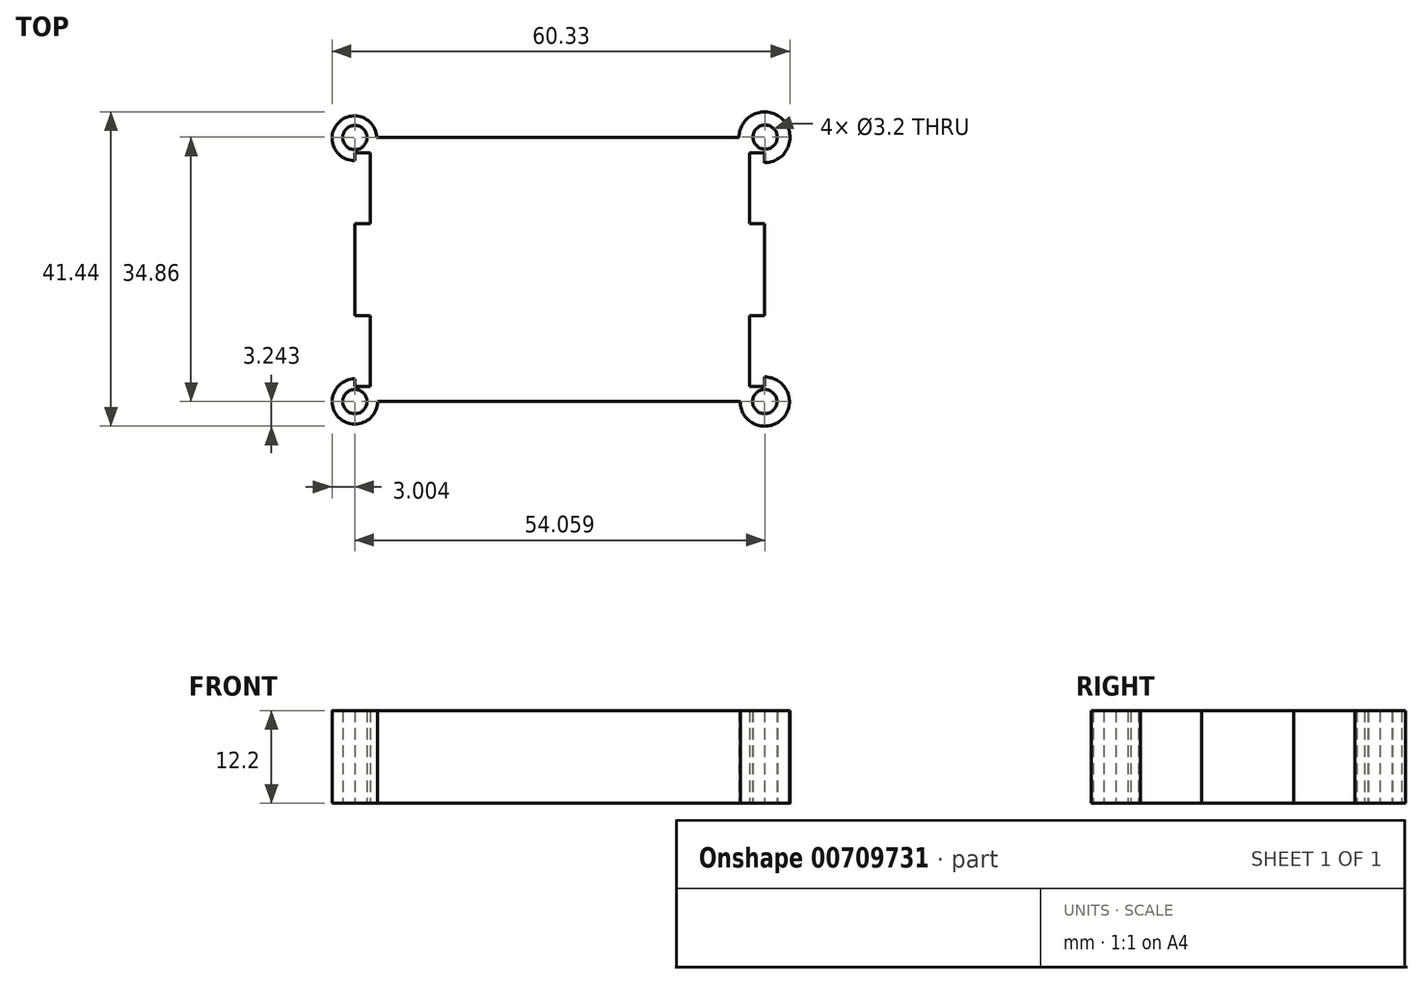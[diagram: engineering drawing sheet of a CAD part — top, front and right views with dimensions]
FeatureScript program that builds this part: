
annotation { "Feature Type Name" : "Feature", "Feature Type Description" : "" }
export const myFeature = defineFeature(function(context is Context, id is Id, definition is map)
    precondition{}
    {
        {
            var Q0;
            Q0=qCreatedBy(makeId("Top.planeOp"),FACE);
            var sketch = newSketch(context, id + "F0", { "sketchPlane" : qUnion([Q0])});
            skLineSegment(sketch, "E0.bottom", {"start": v(-28.95, 12.73) * mm, "end": v(25.05, 12.73) * mm});
            skLineSegment(sketch, "E0.top", {"start": v(-28.95, -22.07) * mm, "end": v(25.05, -22.07) * mm});
            skLineSegment(sketch, "E0.left", {"start": v(-28.95, 12.73) * mm, "end": v(-28.95, -22.07) * mm});
            skLineSegment(sketch, "E0.right", {"start": v(25.05, 12.73) * mm, "end": v(25.05, -22.07) * mm});
            skLineSegment(sketch, "E1", {"start": v(-28.95, 10.73) * mm, "end": v(25.05, 10.73) * mm});
            skLineSegment(sketch, "E2", {"start": v(-28.95, -20.07) * mm, "end": v(25.05, -20.07) * mm});
            skLineSegment(sketch, "E3.bottom", {"start": v(-28.95, 1.4) * mm, "end": v(25.05, 1.4) * mm});
            skLineSegment(sketch, "E3.top", {"start": v(-28.95, 0) * mm, "end": v(25.05, 0) * mm});
            skLineSegment(sketch, "E3.left", {"start": v(-28.95, 1.4) * mm, "end": v(-28.95, 0) * mm});
            skLineSegment(sketch, "E3.right", {"start": v(25.05, 1.4) * mm, "end": v(25.05, 0) * mm});
            skLineSegment(sketch, "E4.bottom", {"start": v(-28.95, -9.33) * mm, "end": v(25.05, -9.33) * mm});
            skLineSegment(sketch, "E4.top", {"start": v(-28.95, -10.73) * mm, "end": v(25.05, -10.73) * mm});
            skLineSegment(sketch, "E4.left", {"start": v(-28.95, -9.33) * mm, "end": v(-28.95, -10.73) * mm});
            skLineSegment(sketch, "E4.right", {"start": v(25.05, -9.33) * mm, "end": v(25.05, -10.73) * mm});
            skLineSegment(sketch, "E5.bottom", {"start": v(-28.95, 12.73) * mm, "end": v(-26.95, 12.73) * mm});
            skLineSegment(sketch, "E5.top", {"start": v(-28.95, -22.07) * mm, "end": v(-26.95, -22.07) * mm});
            skLineSegment(sketch, "E5.right", {"start": v(-26.95, 12.73) * mm, "end": v(-26.95, -22.07) * mm});
            skLineSegment(sketch, "E6.bottom", {"start": v(25.05, 12.73) * mm, "end": v(23.05, 12.73) * mm});
            skLineSegment(sketch, "E6.top", {"start": v(25.05, -22.07) * mm, "end": v(23.05, -22.07) * mm});
            skLineSegment(sketch, "E7", {"start": v(23.05, 12.73) * mm, "end": v(23.05, -22.07) * mm});
            skCircle(sketch, "E8", {"center": v(-28.95, 12.73) * mm, "radius": 1.6 * mm});
            skCircle(sketch, "E9", {"center": v(-28.95, -22.07) * mm, "radius": 1.6 * mm});
            skCircle(sketch, "E10", {"center": v(25.05, -22.07) * mm, "radius": 1.6 * mm});
            skCircle(sketch, "E11", {"center": v(25.11, 12.8) * mm, "radius": 1.6 * mm});
            skArc(sketch, "E12", {"start": v(-26.06, 12.73) * mm, "mid": v(-31.14, 14.68) * mm, "end": v(-28.95, 9.7) * mm});
            skArc(sketch, "E13", {"start": v(21.82, -22.07) * mm, "mid": v(27.36, -24.35) * mm, "end": v(25.05, -18.82) * mm});
            skArc(sketch, "E14", {"start": v(-28.95, -19.06) * mm, "mid": v(-31.08, -24.15) * mm, "end": v(-25.97, -22.07) * mm});
            skArc(sketch, "E15", {"start": v(25.05, 9.42) * mm, "mid": v(27.37, 15.17) * mm, "end": v(21.67, 12.73) * mm});
            skSolve(sketch);
        }
        {
            var Q0;
            {var subQ2=sQuery(id+"F0.wireOp",EDGE,"E13");Q0=makeQuery(id+"F0.imprint","IMPRINT",FACE,{"disambiguationData":[TD([[makeQuery(id+"F0.imprint","IMPRINT",EDGE,{"derivedFrom":subQ2}),1.0]])]});}
            var Q1;
            {var subQ0=sQuery(id+"F0.wireOp",EDGE,"E5.right");var subQ1=sQuery(id+"F0.wireOp",EDGE,"E3.bottom");var subQ2=makeQuery(id+"F0.imprint","INTERSECT",VERTEX,{"derivedFrom":[subQ1,subQ0]});Q1=makeQuery(id+"F0.imprint","IMPRINT",FACE,{"disambiguationData":[TD([[makeQuery(id+"F0.imprint","IMPRINT",EDGE,{"disambiguationData":[TD([[subQ2,-1.0]])],"derivedFrom":subQ1}),-1.0]])]});}
            var Q2;
            {var subQ3=sQuery(id+"F0.wireOp",EDGE,"E1");var subQ5=sQuery(id+"F0.wireOp",EDGE,"E0.left");var subQ6=makeQuery(id+"F0.imprint","INTERSECT",VERTEX,{"derivedFrom":[subQ3,subQ5]});Q2=makeQuery(id+"F0.imprint","IMPRINT",FACE,{"disambiguationData":[TD([[makeQuery(id+"F0.imprint","IMPRINT",EDGE,{"disambiguationData":[TD([[subQ6,-1.0]])],"derivedFrom":subQ3}),1.0]])]});}
            var Q3;
            {var subQ3=sQuery(id+"F0.wireOp",EDGE,"E2");var subQ5=sQuery(id+"F0.wireOp",EDGE,"E0.left");var subQ6=makeQuery(id+"F0.imprint","INTERSECT",VERTEX,{"derivedFrom":[subQ3,subQ5]});Q3=makeQuery(id+"F0.imprint","IMPRINT",FACE,{"disambiguationData":[TD([[makeQuery(id+"F0.imprint","IMPRINT",EDGE,{"disambiguationData":[TD([[subQ6,-1.0]])],"derivedFrom":subQ3}),-1.0]])]});}
            var Q4;
            {var subQ3=sQuery(id+"F0.wireOp",EDGE,"E1");var subQ5=sQuery(id+"F0.wireOp",EDGE,"E0.right");var subQ6=makeQuery(id+"F0.imprint","INTERSECT",VERTEX,{"derivedFrom":[subQ3,subQ5]});Q4=makeQuery(id+"F0.imprint","IMPRINT",FACE,{"disambiguationData":[TD([[makeQuery(id+"F0.imprint","IMPRINT",EDGE,{"disambiguationData":[TD([[subQ6,1.0]])],"derivedFrom":subQ3}),1.0]])]});}
            var Q5;
            {var subQ0=sQuery(id+"F0.wireOp",EDGE,"E5.right");var subQ1=sQuery(id+"F0.wireOp",EDGE,"E1");var subQ2=makeQuery(id+"F0.imprint","INTERSECT",VERTEX,{"derivedFrom":[subQ1,subQ0]});Q5=makeQuery(id+"F0.imprint","IMPRINT",FACE,{"disambiguationData":[TD([[makeQuery(id+"F0.imprint","IMPRINT",EDGE,{"disambiguationData":[TD([[subQ2,-1.0]])],"derivedFrom":subQ1}),-1.0]])]});}
            var Q6;
            {var subQ0=sQuery(id+"F0.wireOp",EDGE,"E0.left");var subQ1=sQuery(id+"F0.wireOp",EDGE,"E1");var subQ2=makeQuery(id+"F0.imprint","INTERSECT",VERTEX,{"derivedFrom":[subQ1,subQ0]});Q6=makeQuery(id+"F0.imprint","IMPRINT",FACE,{"disambiguationData":[TD([[makeQuery(id+"F0.imprint","IMPRINT",EDGE,{"disambiguationData":[TD([[subQ2,-1.0]])],"derivedFrom":subQ1}),-1.0]])]});}
            var Q7;
            {var subQ0=sQuery(id+"F0.wireOp",EDGE,"E5.right");var subQ1=sQuery(id+"F0.wireOp",EDGE,"E3.top");var subQ2=makeQuery(id+"F0.imprint","INTERSECT",VERTEX,{"derivedFrom":[subQ1,subQ0]});Q7=makeQuery(id+"F0.imprint","IMPRINT",FACE,{"disambiguationData":[TD([[makeQuery(id+"F0.imprint","IMPRINT",EDGE,{"disambiguationData":[TD([[subQ2,-1.0]])],"derivedFrom":subQ1}),-1.0]])]});}
            var Q8;
            {var subQ4=sQuery(id+"F0.wireOp",EDGE,"E15");Q8=makeQuery(id+"F0.imprint","IMPRINT",FACE,{"disambiguationData":[TD([[makeQuery(id+"F0.imprint","IMPRINT",EDGE,{"derivedFrom":subQ4}),1.0]])]});}
            var Q9;
            {var subQ0=sQuery(id+"F0.wireOp",EDGE,"E0.right");var subQ1=sQuery(id+"F0.wireOp",EDGE,"E4.bottom");var subQ2=makeQuery(id+"F0.imprint","INTERSECT",VERTEX,{"derivedFrom":[subQ1,subQ0]});Q9=makeQuery(id+"F0.imprint","IMPRINT",FACE,{"disambiguationData":[TD([[makeQuery(id+"F0.imprint","IMPRINT",EDGE,{"disambiguationData":[TD([[subQ2,1.0]])],"derivedFrom":subQ1}),-1.0]])]});}
            var Q10;
            {var subQ4=sQuery(id+"F0.wireOp",EDGE,"E12");Q10=makeQuery(id+"F0.imprint","IMPRINT",FACE,{"disambiguationData":[TD([[makeQuery(id+"F0.imprint","IMPRINT",EDGE,{"derivedFrom":subQ4}),1.0]])]});}
            var Q11;
            {var subQ2=sQuery(id+"F0.wireOp",EDGE,"E14");Q11=makeQuery(id+"F0.imprint","IMPRINT",FACE,{"disambiguationData":[TD([[makeQuery(id+"F0.imprint","IMPRINT",EDGE,{"derivedFrom":subQ2}),1.0]])]});}
            var Q12;
            {var subQ5=sQuery(id+"F0.wireOp",EDGE,"E0.bottom");var subQ8=makeQuery(id+"F0.imprint","INTERSECT",VERTEX,{"derivedFrom":[subQ5,sQuery(id+"F0.wireOp",EDGE,"E12")]});Q12=makeQuery(id+"F0.imprint","IMPRINT",FACE,{"disambiguationData":[TD([[makeQuery(id+"F0.imprint","IMPRINT",EDGE,{"disambiguationData":[TD([[subQ8,-1.0]])],"derivedFrom":subQ5}),-1.0]])]});}
            var Q13;
            {var subQ5=sQuery(id+"F0.wireOp",EDGE,"E0.top");var subQ7=makeQuery(id+"F0.imprint","INTERSECT",VERTEX,{"derivedFrom":[subQ5,sQuery(id+"F0.wireOp",EDGE,"E13")]});Q13=makeQuery(id+"F0.imprint","IMPRINT",FACE,{"disambiguationData":[TD([[makeQuery(id+"F0.imprint","IMPRINT",EDGE,{"disambiguationData":[TD([[subQ7,1.0]])],"derivedFrom":subQ5}),1.0]])]});}
            var Q14;
            {var subQ0=sQuery(id+"F0.wireOp",EDGE,"E0.left");var subQ1=sQuery(id+"F0.wireOp",EDGE,"E3.bottom");var subQ2=makeQuery(id+"F0.imprint","INTERSECT",VERTEX,{"derivedFrom":[subQ1,subQ0]});Q14=makeQuery(id+"F0.imprint","IMPRINT",FACE,{"disambiguationData":[TD([[makeQuery(id+"F0.imprint","IMPRINT",EDGE,{"disambiguationData":[TD([[subQ2,-1.0]])],"derivedFrom":subQ1}),-1.0]])]});}
            var Q15;
            {var subQ0=sQuery(id+"F0.wireOp",EDGE,"E0.right");var subQ1=sQuery(id+"F0.wireOp",EDGE,"E3.bottom");var subQ2=makeQuery(id+"F0.imprint","INTERSECT",VERTEX,{"derivedFrom":[subQ1,subQ0]});Q15=makeQuery(id+"F0.imprint","IMPRINT",FACE,{"disambiguationData":[TD([[makeQuery(id+"F0.imprint","IMPRINT",EDGE,{"disambiguationData":[TD([[subQ2,1.0]])],"derivedFrom":subQ1}),-1.0]])]});}
            var Q16;
            {var subQ0=sQuery(id+"F0.wireOp",EDGE,"E0.left");var subQ1=sQuery(id+"F0.wireOp",EDGE,"E3.top");var subQ2=makeQuery(id+"F0.imprint","INTERSECT",VERTEX,{"derivedFrom":[subQ1,subQ0]});Q16=makeQuery(id+"F0.imprint","IMPRINT",FACE,{"disambiguationData":[TD([[makeQuery(id+"F0.imprint","IMPRINT",EDGE,{"disambiguationData":[TD([[subQ2,-1.0]])],"derivedFrom":subQ1}),-1.0]])]});}
            var Q17;
            {var subQ0=sQuery(id+"F0.wireOp",EDGE,"E0.right");var subQ1=sQuery(id+"F0.wireOp",EDGE,"E3.top");var subQ2=makeQuery(id+"F0.imprint","INTERSECT",VERTEX,{"derivedFrom":[subQ1,subQ0]});Q17=makeQuery(id+"F0.imprint","IMPRINT",FACE,{"disambiguationData":[TD([[makeQuery(id+"F0.imprint","IMPRINT",EDGE,{"disambiguationData":[TD([[subQ2,1.0]])],"derivedFrom":subQ1}),-1.0]])]});}
            var Q18;
            {var subQ0=sQuery(id+"F0.wireOp",EDGE,"E0.left");var subQ1=sQuery(id+"F0.wireOp",EDGE,"E4.bottom");var subQ2=makeQuery(id+"F0.imprint","INTERSECT",VERTEX,{"derivedFrom":[subQ1,subQ0]});Q18=makeQuery(id+"F0.imprint","IMPRINT",FACE,{"disambiguationData":[TD([[makeQuery(id+"F0.imprint","IMPRINT",EDGE,{"disambiguationData":[TD([[subQ2,-1.0]])],"derivedFrom":subQ1}),-1.0]])]});}
            var Q19;
            {var subQ0=sQuery(id+"F0.wireOp",EDGE,"E5.right");var subQ1=sQuery(id+"F0.wireOp",EDGE,"E2");var subQ2=makeQuery(id+"F0.imprint","INTERSECT",VERTEX,{"derivedFrom":[subQ1,subQ0]});Q19=makeQuery(id+"F0.imprint","IMPRINT",FACE,{"disambiguationData":[TD([[makeQuery(id+"F0.imprint","IMPRINT",EDGE,{"disambiguationData":[TD([[subQ2,-1.0]])],"derivedFrom":subQ1}),1.0]])]});}
            var Q20;
            {var subQ3=sQuery(id+"F0.wireOp",EDGE,"E2");var subQ5=sQuery(id+"F0.wireOp",EDGE,"E0.right");var subQ6=makeQuery(id+"F0.imprint","INTERSECT",VERTEX,{"derivedFrom":[subQ3,subQ5]});Q20=makeQuery(id+"F0.imprint","IMPRINT",FACE,{"disambiguationData":[TD([[makeQuery(id+"F0.imprint","IMPRINT",EDGE,{"disambiguationData":[TD([[subQ6,1.0]])],"derivedFrom":subQ3}),-1.0]])]});}
            var Q21;
            {var subQ0=sQuery(id+"F0.wireOp",EDGE,"E0.left");var subQ4=sQuery(id+"F0.wireOp",EDGE,"E2");var subQ5=makeQuery(id+"F0.imprint","INTERSECT",VERTEX,{"derivedFrom":[subQ4,subQ0]});Q21=makeQuery(id+"F0.imprint","IMPRINT",FACE,{"disambiguationData":[TD([[makeQuery(id+"F0.imprint","IMPRINT",EDGE,{"disambiguationData":[TD([[subQ5,-1.0]])],"derivedFrom":subQ4}),1.0]])]});}
            var Q22;
            {var subQ0=sQuery(id+"F0.wireOp",EDGE,"E0.right");var subQ1=sQuery(id+"F0.wireOp",EDGE,"E1");var subQ2=makeQuery(id+"F0.imprint","INTERSECT",VERTEX,{"derivedFrom":[subQ1,subQ0]});Q22=makeQuery(id+"F0.imprint","IMPRINT",FACE,{"disambiguationData":[TD([[makeQuery(id+"F0.imprint","IMPRINT",EDGE,{"disambiguationData":[TD([[subQ2,1.0]])],"derivedFrom":subQ1}),-1.0]])]});}
            var Q23;
            {var subQ0=sQuery(id+"F0.wireOp",EDGE,"E5.right");var subQ1=sQuery(id+"F0.wireOp",EDGE,"E4.bottom");var subQ2=makeQuery(id+"F0.imprint","INTERSECT",VERTEX,{"derivedFrom":[subQ1,subQ0]});Q23=makeQuery(id+"F0.imprint","IMPRINT",FACE,{"disambiguationData":[TD([[makeQuery(id+"F0.imprint","IMPRINT",EDGE,{"disambiguationData":[TD([[subQ2,-1.0]])],"derivedFrom":subQ1}),-1.0]])]});}
            var Q24;
            {var subQ0=sQuery(id+"F0.wireOp",EDGE,"E0.right");var subQ4=sQuery(id+"F0.wireOp",EDGE,"E2");var subQ5=makeQuery(id+"F0.imprint","INTERSECT",VERTEX,{"derivedFrom":[subQ4,subQ0]});Q24=makeQuery(id+"F0.imprint","IMPRINT",FACE,{"disambiguationData":[TD([[makeQuery(id+"F0.imprint","IMPRINT",EDGE,{"disambiguationData":[TD([[subQ5,1.0]])],"derivedFrom":subQ4}),1.0]])]});}
            extrude(context, id + "F1", {"entities" : qUnion([Q0, Q1, Q2, Q3, Q4, Q5, Q6, Q7, Q8, Q9, Q10, Q11, Q12, Q13, Q14, Q15, Q16, Q17, Q18, Q19, Q20, Q21, Q22, Q23, Q24]), "depth" : 2 * mm, "offsetDistance" : 25 * mm});
        }
        {
            var Q0;
            {var subQ5=sQuery(id+"F0.wireOp",EDGE,"E0.bottom");var subQ8=makeQuery(id+"F0.imprint","INTERSECT",VERTEX,{"derivedFrom":[subQ5,sQuery(id+"F0.wireOp",EDGE,"E12")]});Q0=makeQuery(id+"F0.imprint","IMPRINT",FACE,{"disambiguationData":[TD([[makeQuery(id+"F0.imprint","IMPRINT",EDGE,{"disambiguationData":[TD([[subQ8,-1.0]])],"derivedFrom":subQ5}),-1.0]])]});}
            var Q1;
            {var subQ0=sQuery(id+"F0.wireOp",EDGE,"E0.left");var subQ1=sQuery(id+"F0.wireOp",EDGE,"E1");var subQ2=makeQuery(id+"F0.imprint","INTERSECT",VERTEX,{"derivedFrom":[subQ1,subQ0]});Q1=makeQuery(id+"F0.imprint","IMPRINT",FACE,{"disambiguationData":[TD([[makeQuery(id+"F0.imprint","IMPRINT",EDGE,{"disambiguationData":[TD([[subQ2,-1.0]])],"derivedFrom":subQ1}),-1.0]])]});}
            var Q2;
            {var subQ0=sQuery(id+"F0.wireOp",EDGE,"E0.left");var subQ1=sQuery(id+"F0.wireOp",EDGE,"E3.top");var subQ2=makeQuery(id+"F0.imprint","INTERSECT",VERTEX,{"derivedFrom":[subQ1,subQ0]});Q2=makeQuery(id+"F0.imprint","IMPRINT",FACE,{"disambiguationData":[TD([[makeQuery(id+"F0.imprint","IMPRINT",EDGE,{"disambiguationData":[TD([[subQ2,-1.0]])],"derivedFrom":subQ1}),-1.0]])]});}
            var Q3;
            {var subQ0=sQuery(id+"F0.wireOp",EDGE,"E0.left");var subQ4=sQuery(id+"F0.wireOp",EDGE,"E2");var subQ5=makeQuery(id+"F0.imprint","INTERSECT",VERTEX,{"derivedFrom":[subQ4,subQ0]});Q3=makeQuery(id+"F0.imprint","IMPRINT",FACE,{"disambiguationData":[TD([[makeQuery(id+"F0.imprint","IMPRINT",EDGE,{"disambiguationData":[TD([[subQ5,-1.0]])],"derivedFrom":subQ4}),1.0]])]});}
            var Q4;
            {var subQ5=sQuery(id+"F0.wireOp",EDGE,"E0.top");var subQ7=makeQuery(id+"F0.imprint","INTERSECT",VERTEX,{"derivedFrom":[subQ5,sQuery(id+"F0.wireOp",EDGE,"E13")]});Q4=makeQuery(id+"F0.imprint","IMPRINT",FACE,{"disambiguationData":[TD([[makeQuery(id+"F0.imprint","IMPRINT",EDGE,{"disambiguationData":[TD([[subQ7,1.0]])],"derivedFrom":subQ5}),1.0]])]});}
            var Q5;
            {var subQ0=sQuery(id+"F0.wireOp",EDGE,"E0.right");var subQ4=sQuery(id+"F0.wireOp",EDGE,"E2");var subQ5=makeQuery(id+"F0.imprint","INTERSECT",VERTEX,{"derivedFrom":[subQ4,subQ0]});Q5=makeQuery(id+"F0.imprint","IMPRINT",FACE,{"disambiguationData":[TD([[makeQuery(id+"F0.imprint","IMPRINT",EDGE,{"disambiguationData":[TD([[subQ5,1.0]])],"derivedFrom":subQ4}),1.0]])]});}
            var Q6;
            {var subQ0=sQuery(id+"F0.wireOp",EDGE,"E0.right");var subQ1=sQuery(id+"F0.wireOp",EDGE,"E3.top");var subQ2=makeQuery(id+"F0.imprint","INTERSECT",VERTEX,{"derivedFrom":[subQ1,subQ0]});Q6=makeQuery(id+"F0.imprint","IMPRINT",FACE,{"disambiguationData":[TD([[makeQuery(id+"F0.imprint","IMPRINT",EDGE,{"disambiguationData":[TD([[subQ2,1.0]])],"derivedFrom":subQ1}),-1.0]])]});}
            var Q7;
            {var subQ0=sQuery(id+"F0.wireOp",EDGE,"E0.right");var subQ1=sQuery(id+"F0.wireOp",EDGE,"E4.bottom");var subQ2=makeQuery(id+"F0.imprint","INTERSECT",VERTEX,{"derivedFrom":[subQ1,subQ0]});Q7=makeQuery(id+"F0.imprint","IMPRINT",FACE,{"disambiguationData":[TD([[makeQuery(id+"F0.imprint","IMPRINT",EDGE,{"disambiguationData":[TD([[subQ2,1.0]])],"derivedFrom":subQ1}),-1.0]])]});}
            var Q8;
            {var subQ0=sQuery(id+"F0.wireOp",EDGE,"E0.left");var subQ1=sQuery(id+"F0.wireOp",EDGE,"E4.bottom");var subQ2=makeQuery(id+"F0.imprint","INTERSECT",VERTEX,{"derivedFrom":[subQ1,subQ0]});Q8=makeQuery(id+"F0.imprint","IMPRINT",FACE,{"disambiguationData":[TD([[makeQuery(id+"F0.imprint","IMPRINT",EDGE,{"disambiguationData":[TD([[subQ2,-1.0]])],"derivedFrom":subQ1}),-1.0]])]});}
            var Q9;
            {var subQ0=sQuery(id+"F0.wireOp",EDGE,"E0.right");var subQ1=sQuery(id+"F0.wireOp",EDGE,"E1");var subQ2=makeQuery(id+"F0.imprint","INTERSECT",VERTEX,{"derivedFrom":[subQ1,subQ0]});Q9=makeQuery(id+"F0.imprint","IMPRINT",FACE,{"disambiguationData":[TD([[makeQuery(id+"F0.imprint","IMPRINT",EDGE,{"disambiguationData":[TD([[subQ2,1.0]])],"derivedFrom":subQ1}),-1.0]])]});}
            var Q10;
            {var subQ0=sQuery(id+"F0.wireOp",EDGE,"E0.right");var subQ1=sQuery(id+"F0.wireOp",EDGE,"E3.bottom");var subQ2=makeQuery(id+"F0.imprint","INTERSECT",VERTEX,{"derivedFrom":[subQ1,subQ0]});Q10=makeQuery(id+"F0.imprint","IMPRINT",FACE,{"disambiguationData":[TD([[makeQuery(id+"F0.imprint","IMPRINT",EDGE,{"disambiguationData":[TD([[subQ2,1.0]])],"derivedFrom":subQ1}),-1.0]])]});}
            var Q11;
            {var subQ0=sQuery(id+"F0.wireOp",EDGE,"E0.left");var subQ1=sQuery(id+"F0.wireOp",EDGE,"E3.bottom");var subQ2=makeQuery(id+"F0.imprint","INTERSECT",VERTEX,{"derivedFrom":[subQ1,subQ0]});Q11=makeQuery(id+"F0.imprint","IMPRINT",FACE,{"disambiguationData":[TD([[makeQuery(id+"F0.imprint","IMPRINT",EDGE,{"disambiguationData":[TD([[subQ2,-1.0]])],"derivedFrom":subQ1}),-1.0]])]});}
            var Q12;
            {var subQ4=sQuery(id+"F0.wireOp",EDGE,"E15");Q12=makeQuery(id+"F0.imprint","IMPRINT",FACE,{"disambiguationData":[TD([[makeQuery(id+"F0.imprint","IMPRINT",EDGE,{"derivedFrom":subQ4}),1.0]])]});}
            var Q13;
            {var subQ2=sQuery(id+"F0.wireOp",EDGE,"E13");Q13=makeQuery(id+"F0.imprint","IMPRINT",FACE,{"disambiguationData":[TD([[makeQuery(id+"F0.imprint","IMPRINT",EDGE,{"derivedFrom":subQ2}),1.0]])]});}
            var Q14;
            {var subQ3=sQuery(id+"F0.wireOp",EDGE,"E2");var subQ5=sQuery(id+"F0.wireOp",EDGE,"E0.right");var subQ6=makeQuery(id+"F0.imprint","INTERSECT",VERTEX,{"derivedFrom":[subQ3,subQ5]});Q14=makeQuery(id+"F0.imprint","IMPRINT",FACE,{"disambiguationData":[TD([[makeQuery(id+"F0.imprint","IMPRINT",EDGE,{"disambiguationData":[TD([[subQ6,1.0]])],"derivedFrom":subQ3}),-1.0]])]});}
            var Q15;
            {var subQ3=sQuery(id+"F0.wireOp",EDGE,"E1");var subQ5=sQuery(id+"F0.wireOp",EDGE,"E0.right");var subQ6=makeQuery(id+"F0.imprint","INTERSECT",VERTEX,{"derivedFrom":[subQ3,subQ5]});Q15=makeQuery(id+"F0.imprint","IMPRINT",FACE,{"disambiguationData":[TD([[makeQuery(id+"F0.imprint","IMPRINT",EDGE,{"disambiguationData":[TD([[subQ6,1.0]])],"derivedFrom":subQ3}),1.0]])]});}
            var Q16;
            {var subQ3=sQuery(id+"F0.wireOp",EDGE,"E2");var subQ5=sQuery(id+"F0.wireOp",EDGE,"E0.left");var subQ6=makeQuery(id+"F0.imprint","INTERSECT",VERTEX,{"derivedFrom":[subQ3,subQ5]});Q16=makeQuery(id+"F0.imprint","IMPRINT",FACE,{"disambiguationData":[TD([[makeQuery(id+"F0.imprint","IMPRINT",EDGE,{"disambiguationData":[TD([[subQ6,-1.0]])],"derivedFrom":subQ3}),-1.0]])]});}
            var Q17;
            {var subQ2=sQuery(id+"F0.wireOp",EDGE,"E14");Q17=makeQuery(id+"F0.imprint","IMPRINT",FACE,{"disambiguationData":[TD([[makeQuery(id+"F0.imprint","IMPRINT",EDGE,{"derivedFrom":subQ2}),1.0]])]});}
            var Q18;
            {var subQ4=sQuery(id+"F0.wireOp",EDGE,"E12");Q18=makeQuery(id+"F0.imprint","IMPRINT",FACE,{"disambiguationData":[TD([[makeQuery(id+"F0.imprint","IMPRINT",EDGE,{"derivedFrom":subQ4}),1.0]])]});}
            var Q19;
            {var subQ3=sQuery(id+"F0.wireOp",EDGE,"E1");var subQ5=sQuery(id+"F0.wireOp",EDGE,"E0.left");var subQ6=makeQuery(id+"F0.imprint","INTERSECT",VERTEX,{"derivedFrom":[subQ3,subQ5]});Q19=makeQuery(id+"F0.imprint","IMPRINT",FACE,{"disambiguationData":[TD([[makeQuery(id+"F0.imprint","IMPRINT",EDGE,{"disambiguationData":[TD([[subQ6,-1.0]])],"derivedFrom":subQ3}),1.0]])]});}
            extrude(context, id + "F2", {"entities" : qUnion([Q0, Q1, Q2, Q3, Q4, Q5, Q6, Q7, Q8, Q9, Q10, Q11, Q12, Q13, Q14, Q15, Q16, Q17, Q18, Q19]), "operationType" : NewBodyOperationType.ADD, "depth" : 12.2 * mm, "offsetDistance" : 25 * mm});
        }
        {
            var Q0;
            {var subQ0=sQuery(id+"F0.wireOp",EDGE,"E5.right");var subQ1=sQuery(id+"F0.wireOp",EDGE,"E3.bottom");var subQ2=makeQuery(id+"F0.imprint","INTERSECT",VERTEX,{"derivedFrom":[subQ1,subQ0]});Q0=makeQuery(id+"F0.imprint","IMPRINT",FACE,{"disambiguationData":[TD([[makeQuery(id+"F0.imprint","IMPRINT",EDGE,{"disambiguationData":[TD([[subQ2,-1.0]])],"derivedFrom":subQ1}),-1.0]])]});}
            var Q1;
            {var subQ0=sQuery(id+"F0.wireOp",EDGE,"E5.right");var subQ1=sQuery(id+"F0.wireOp",EDGE,"E4.bottom");var subQ2=makeQuery(id+"F0.imprint","INTERSECT",VERTEX,{"derivedFrom":[subQ1,subQ0]});Q1=makeQuery(id+"F0.imprint","IMPRINT",FACE,{"disambiguationData":[TD([[makeQuery(id+"F0.imprint","IMPRINT",EDGE,{"disambiguationData":[TD([[subQ2,-1.0]])],"derivedFrom":subQ1}),-1.0]])]});}
            extrude(context, id + "F3", {"entities" : qUnion([Q0, Q1]), "operationType" : NewBodyOperationType.ADD, "depth" : 4.4 * mm, "offsetDistance" : 25 * mm});
        }
    });
